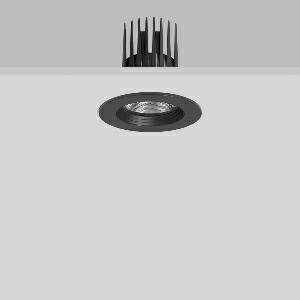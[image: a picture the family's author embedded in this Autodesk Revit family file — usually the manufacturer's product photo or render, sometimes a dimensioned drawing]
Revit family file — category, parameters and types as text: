
# Revit family: heledon_mini_e_901742_003_2_76_5036
name_source: partatom
category: Lighting Fixtures
units: mm (PartAtom-declared; Revit-internal decimal feet)

## family parameters
Cut with Voids When Loaded = No
Host = Face
Light Source = No
Part Type = Normal
Room Calculation Point = No
Round Connector Dimension = Use Diameter
Shared = No

## types (1)
- HELEDON mini E (1 x LED Modul 927, 2400 lm, 2700)
    Apparent Load = 20 VA
    Approval mark = CE
    CIE Flux Codes = 95 99 100 100 100
    Color Rendering = 92
    Color Temperature = 2700
    Default Elevation = 1800 mm
    Description = Series: HELEDON mini
Round recessed downlight. Housing: die-cast aluminium, powder-coated. Black plastic ring and recessed LED to prevent glare from the side. Optical assembly with reflector made of MIRO-Silver with 98% total light reflection for outstanding efficiency - can be changed without tools. Best colour rendering index Ra>90. Suitable for Recessed ceiling mounting. Installation without tools thanks to spring fastening system. Including separate LED converter with connecting cable 600 mm.High quality converter without flickering and stroboscopic effect. Through-wiring box (5 pole) available as accessory. The following accessories can be mounted without use of tools: interchangeable lenses, decorative glasses, honeycomb louvre, clear and frosted diffusers, white interchangeable plastic ring. 
Colour: deep black, matt (RAL 9005)
Diameter: 124 mm
Height: 3 mm
Cut-out diameter: 114 mm
Recess height: 170 mm
Luminaire: recess height: 120 mm
Lamp: LED
Socket: without socket
Colour temperature: 2700K
Colour rendering index (CRI): 92
System power: 20 W
Rated luminous flux: 2400 lm
Luminous efficiency: 120 lm/W
Control gear: Converter, dimmable, DALI
Protection class: II
Type of protection: IP 20
    Height = 0 mm  [stored 0 ft]
    Lamp = 1 x LED Modul 927
    Lamp Light Flux = 2400 lm
    Lamp count = 1
    Length = 124 mm  [stored 0.406824 ft]
    Lifetime = 50000 h
    Luminous efficacy = 120 lm/W
    Manufacturer = RZB
    ModVariant = No
    Model = 901742.003.2.76
    Mounting Place = Ceiling
    Mounting Type = Recessed
    Number of Poles = 1
    OnlyDefault = Yes
    Power Factor = 1
    Product Name = HELEDON mini E
    Product group = Recessed downlights
    ProductGroupID = 402
    Protection Class = Protection class II
    Protection Degree = IP 20
    RLX_Detail_Level = 1
    RLX_Emergency_Light_Flux = 0 lm
    RLX_Emergency_Type = 0
    RLX_Emergency_Type_DB = No
    RlxData = <blob elided: 124857 chars, md5=ee2fd19f>
    Socket = socket
    Standby Power = 0 W
    System Light Flux = 2400 lm
    System Power = 20 W
    Type Comments = Product without accessories
    Type Image = 901657.003.jpg
    URL = http://relux.com
    VarID = ---
    Voltage = 230 V
    Voltage Range = 220-240 V
    Weight = 0.00 kg
    Width = 0 mm  [stored 0 ft]

note: [stored X ft] marks values corroborated as IEEE doubles in the binary element streams (Revit-internal decimal feet)

## geometry (parser evidence)
native form markers: Blend x4, Sweep x11
no freeform markers — native parametric forms only
